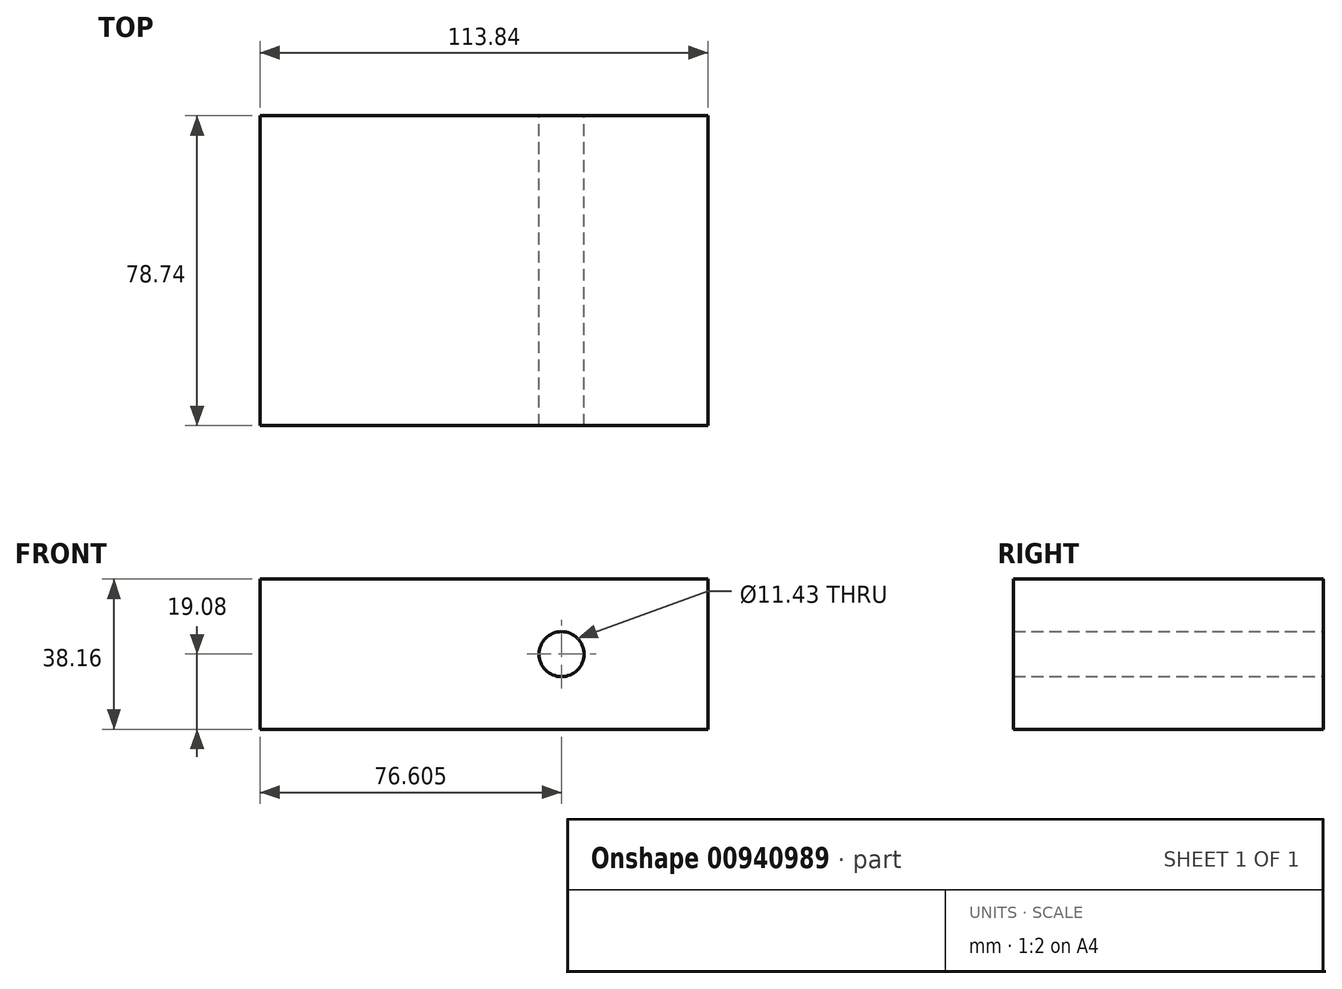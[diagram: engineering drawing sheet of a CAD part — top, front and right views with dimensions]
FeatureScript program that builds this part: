
annotation { "Feature Type Name" : "Feature", "Feature Type Description" : "" }
export const myFeature = defineFeature(function(context is Context, id is Id, definition is map)
    precondition{}
    {
        {
            var Q0;
            Q0=qCreatedBy(makeId("Front.planeOp"),FACE);
            var sketch = newSketch(context, id + "F0", { "sketchPlane" : qUnion([Q0])});
            skLineSegment(sketch, "E0.bottom", {"start": v(56.92, 19.08) * mm, "end": v(-56.92, 19.08) * mm});
            skLineSegment(sketch, "E0.top", {"start": v(56.92, -19.08) * mm, "end": v(-56.92, -19.08) * mm});
            skLineSegment(sketch, "E0.left", {"start": v(56.92, 19.08) * mm, "end": v(56.92, -19.08) * mm});
            skLineSegment(sketch, "E0.right", {"start": v(-56.92, 19.08) * mm, "end": v(-56.92, -19.08) * mm});
            skPoint(sketch, "E0.middle", {"position": v(0, 0) * mm});
            skCircle(sketch, "E1", {"center": v(-19.69, 0) * mm, "radius": 5.72 * mm});
            skCircle(sketch, "E2.MirrorC", {"center": v(19.69, 0) * mm, "radius": 5.72 * mm});
            skSolve(sketch);
        }
        {
            var Q0;
            Q0=makeQuery(id+"F0.imprint","IMPRINT",FACE,{"disambiguationData":[TD([[makeQuery(id+"F0.imprint","IMPRINT",EDGE,{"derivedFrom":sQuery(id+"F0.wireOp",EDGE,"E0.bottom")}),1.0]])]});
            extrude(context, id + "F1", {"entities" : qUnion([Q0]), "depth" : 25.4 * mm, "offsetDistance" : 25.4 * mm});
        }
        {
            var Q0;
            Q0=makeQuery(id+"F0.imprint","IMPRINT",FACE,{"disambiguationData":[TD([[makeQuery(id+"F0.imprint","IMPRINT",EDGE,{"derivedFrom":sQuery(id+"F0.wireOp",EDGE,"E1")}),1.0]])]});
            var Q1;
            Q1=makeQuery(id+"F0.imprint","IMPRINT",FACE,{"disambiguationData":[TD([[makeQuery(id+"F0.imprint","IMPRINT",EDGE,{"derivedFrom":sQuery(id+"F0.wireOp",EDGE,"E2.MirrorC")}),-1.0]])]});
            extrude(context, id + "F2", {"entities" : qUnion([Q0, Q1]), "operationType" : NewBodyOperationType.ADD, "depth" : 78.74 * mm, "offsetDistance" : 25.4 * mm});
        }
    });
